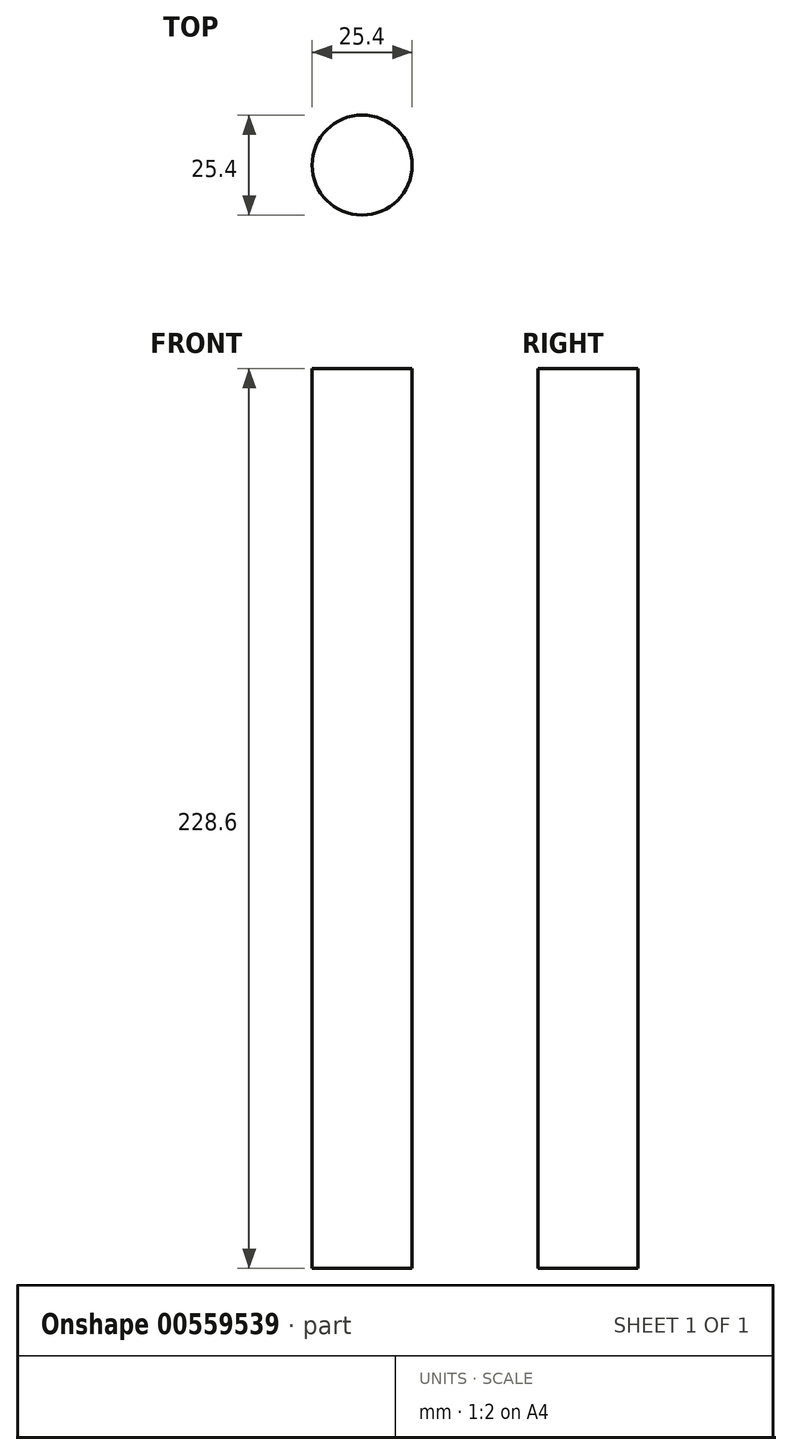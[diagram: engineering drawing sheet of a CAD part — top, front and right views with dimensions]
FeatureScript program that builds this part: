
annotation { "Feature Type Name" : "Feature", "Feature Type Description" : "" }
export const myFeature = defineFeature(function(context is Context, id is Id, definition is map)
    precondition{}
    {
        {
            var Q0;
            Q0=qCreatedBy(makeId("Top.planeOp"),FACE);
            var sketch = newSketch(context, id + "F0", { "sketchPlane" : qUnion([Q0])});
            skCircle(sketch, "E0", {"center": v(0, 0) * mm, "radius": 12.7 * mm});
            skSolve(sketch);
        }
        {
            var Q0;
            Q0=makeQuery(id+"F0.imprint","IMPRINT",FACE,{"disambiguationData":[TD([[makeQuery(id+"F0.imprint","IMPRINT",EDGE,{"derivedFrom":sQuery(id+"F0.wireOp",EDGE,"E0")}),1.0]])]});
            var Q1;
            Q1=sQuery(id+"F0.wireOp",EDGE,"E0");
            extrude(context, id + "F1", {"entities" : qUnion([Q0]), "bodyType" : ToolBodyType.SURFACE, "surfaceEntities" : qUnion([Q1]), "depth" : 228.6 * mm, "offsetDistance" : 25.4 * mm});
        }
    });
